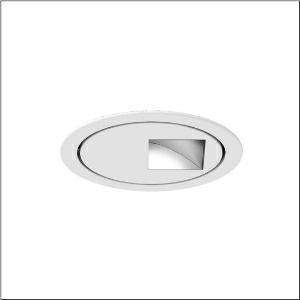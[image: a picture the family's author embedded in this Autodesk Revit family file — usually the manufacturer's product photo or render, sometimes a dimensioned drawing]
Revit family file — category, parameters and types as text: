
# Revit family: lunis_11_mini_round_51dk11cd2wf21
name_source: partatom
category: Lighting Fixtures
units: mm (PartAtom-declared; Revit-internal decimal feet)

## family parameters
Cut with Voids When Loaded = No
Host = Face
Light Source = No
Part Type = Normal
Room Calculation Point = No
Round Connector Dimension = Use Diameter
Shared = No

## types (1)
- Lunis 11 mini round (1 x LED 3000K / CRI = 80 (unbekannt), 2380 lm, 3000K)
    Apparent Load = 28 VA
    CIE Flux Codes = 44 77 97 100 100
    Color Rendering = 80
    Color Temperature = 3000K
    Default Elevation = 1800 mm
    Description = Lunis 11 mini round, downlight, light control with wallwasher, of highly reflective aluminium, highly specular, light emission: direct distribution, LED rated luminous flux: 2.380lm, light colour: 830, control gear: ECG, with terminal, 5-pole, mains connection: 220..230V, AC/DC, 0/50..60Hz, LED module, luminaire module, of aluminium, highly specular, white, diameter: 176mm, clamping range: 1..40mm, recessing ring, of plastic, traffic white (RAL 9016), protection rating (complete): IP20, insulation class (complete): insulation class II (safety insulation), certification: CE, permissible ambient temperature for indoor applications: 0..+35°C, packaging unit: 1 piece
    Height = 0 mm  [stored 0 ft]
    Lamp = 1 x LED 3000K / CRI >= 80 (unbekannt)
    Lamp Light Flux = 2380 lm
    Lamp count = 1
    Length = 176 mm
    Luminous efficacy = 86 lm/W
    Manufacturer = Siteco
    ModVariant = No
    Model = 51DK11CD2WF21
    Mounting Place = Ceiling
    Mounting Type = Recessed
    Number of Poles = 1
    OnlyDefault = Yes
    Power Factor = 1
    Product Name = Lunis 11 mini round
    Product group = downlight
    ProductGroupID = 400
    Protection Class = Protection class II
    Protection Degree = IP 20
    RLX_Detail_Level = 1
    RLX_Emergency_Light_Flux = 0 lm
    RLX_Emergency_Type = 0
    RLX_Emergency_Type_DB = No
    RlxData = <blob elided: 59497 chars, md5=b16ad5e8>
    Socket = socket
    Standby Power = 0 W
    System Light Flux = 2380 lm
    System Power = 28 W
    Type Comments = Product without accessories
    Type Image = l_1004772.jpg
    URL = http://relux.com
    VarID = ---
    Voltage = 0 V
    Weight = 0.00 kg
    Width = 176 mm

note: [stored X ft] marks values corroborated as IEEE doubles in the binary element streams (Revit-internal decimal feet)

## geometry (parser evidence)
native form markers: Blend x4, Sweep x10
no freeform markers — native parametric forms only
